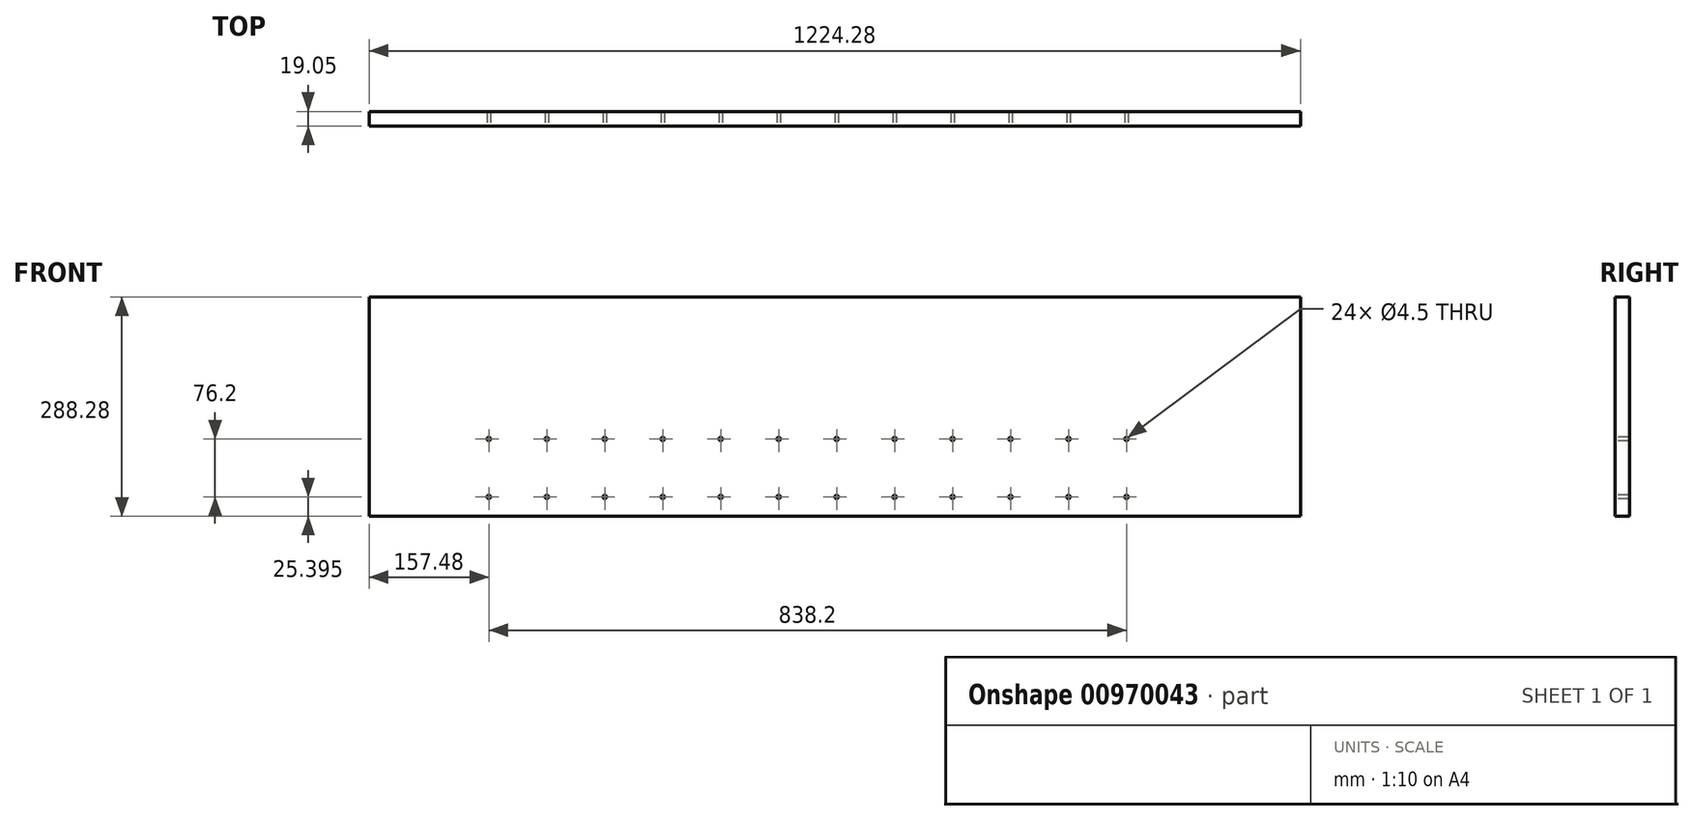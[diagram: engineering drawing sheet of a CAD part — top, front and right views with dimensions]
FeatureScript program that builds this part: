
annotation { "Feature Type Name" : "Feature", "Feature Type Description" : "" }
export const myFeature = defineFeature(function(context is Context, id is Id, definition is map)
    precondition{}
    {
        {
            var Q0;
            Q0=qCreatedBy(makeId("Front.planeOp"),FACE);
            var sketch = newSketch(context, id + "F0", { "sketchPlane" : qUnion([Q0])});
            skLineSegment(sketch, "E0.bottom", {"start": v(612.14, -144.14) * mm, "end": v(-612.14, -144.15) * mm});
            skLineSegment(sketch, "E0.top", {"start": v(612.14, 144.15) * mm, "end": v(-612.14, 144.15) * mm});
            skLineSegment(sketch, "E0.left", {"start": v(612.14, -144.14) * mm, "end": v(612.14, 144.15) * mm});
            skLineSegment(sketch, "E0.right", {"start": v(-612.14, -144.15) * mm, "end": v(-612.14, 144.14) * mm});
            skPoint(sketch, "E0.middle", {"position": v(0, 0) * mm});
            skSolve(sketch);
        }
        {
            var Q0;
            Q0=makeQuery(id+"F0.imprint","IMPRINT",FACE,{"disambiguationData":[TD([[makeQuery(id+"F0.imprint","IMPRINT",EDGE,{"derivedFrom":sQuery(id+"F0.wireOp",EDGE,"E0.bottom")}),-1.0]])]});
            extrude(context, id + "F1", {"entities" : qUnion([Q0]), "depth" : 19.05 * mm, "offsetDistance" : 25.4 * mm});
        }
        {
            var Q0;
            Q0=makeQuery(id+"F1.opExtrude","CAP_FACE",FACE,{"disambiguationData":[OSD([sQuery(id+"F0.wireOp",EDGE,"E0.bottom"),sQuery(id+"F0.wireOp",EDGE,"E0.top"),sQuery(id+"F0.wireOp",EDGE,"E0.left"),sQuery(id+"F0.wireOp",EDGE,"E0.right")])],"isStart":false});
            var sketch = newSketch(context, id + "F2", { "sketchPlane" : qUnion([Q0])});
            skLineSegment(sketch, "E1", {"start": v(-496.57, 144.15) * mm, "end": v(-496.57, -144.15) * mm, "construction": true});
            skLineSegment(sketch, "E2", {"start": v(425.45, 144.15) * mm, "end": v(425.45, -144.14) * mm, "construction": true});
            skLineSegment(sketch, "E3", {"start": v(-496.57, -42.55) * mm, "end": v(425.45, -42.55) * mm, "construction": true});
            skLineSegment(sketch, "E4", {"start": v(-35.56, -42.55) * mm, "end": v(-35.56, 387.93) * mm, "construction": true});
            skLineSegment(sketch, "E5", {"start": v(-35.56, -42.55) * mm, "end": v(-35.56, -118.75) * mm, "construction": true});
            skLineSegment(sketch, "E6", {"start": v(-496.57, -118.75) * mm, "end": v(425.45, -118.75) * mm, "construction": true});
            skLineSegment(sketch, "E7", {"start": v(-35.56, -80.65) * mm, "end": v(425.45, -80.65) * mm, "construction": true});
            skPoint(sketch, "E8", {"position": v(2.54, -42.55) * mm});
            skPoint(sketch, "E9", {"position": v(78.74, -42.55) * mm});
            skPoint(sketch, "E10", {"position": v(231.14, -42.55) * mm});
            skPoint(sketch, "E11", {"position": v(154.94, -42.55) * mm});
            skPoint(sketch, "E12", {"position": v(307.34, -42.55) * mm});
            skPoint(sketch, "E13", {"position": v(383.54, -42.55) * mm});
            skPoint(sketch, "E14.MirrorP", {"position": v(2.54, -118.75) * mm});
            skPoint(sketch, "E15.MirrorP", {"position": v(78.74, -118.75) * mm});
            skPoint(sketch, "E16.MirrorP", {"position": v(154.94, -118.75) * mm});
            skPoint(sketch, "E17.MirrorP", {"position": v(231.14, -118.75) * mm});
            skPoint(sketch, "E18.MirrorP", {"position": v(307.34, -118.75) * mm});
            skPoint(sketch, "E19.MirrorP", {"position": v(383.54, -118.75) * mm});
            skPoint(sketch, "E20.MirrorP", {"position": v(-73.66, -42.55) * mm});
            skPoint(sketch, "E21.MirrorP", {"position": v(-73.66, -118.75) * mm});
            skPoint(sketch, "E22.MirrorP", {"position": v(-149.86, -118.75) * mm});
            skPoint(sketch, "E23.MirrorP", {"position": v(-149.86, -42.55) * mm});
            skPoint(sketch, "E24.MirrorP", {"position": v(-226.06, -42.55) * mm});
            skPoint(sketch, "E25.MirrorP", {"position": v(-226.06, -118.75) * mm});
            skPoint(sketch, "E26.MirrorP", {"position": v(-302.26, -118.75) * mm});
            skPoint(sketch, "E27.MirrorP", {"position": v(-302.26, -42.55) * mm});
            skPoint(sketch, "E28.MirrorP", {"position": v(-378.46, -42.55) * mm});
            skPoint(sketch, "E29.MirrorP", {"position": v(-378.46, -118.75) * mm});
            skPoint(sketch, "E30.MirrorP", {"position": v(-454.66, -118.75) * mm});
            skPoint(sketch, "E31.MirrorP", {"position": v(-454.66, -42.55) * mm});
            skSolve(sketch);
        }
        {
            var Q0;
            Q0=sQuery(id+"F2.wireOp",VERTEX,"E13");
            var Q1;
            Q1=sQuery(id+"F2.wireOp",VERTEX,"E12");
            var Q2;
            Q2=sQuery(id+"F2.wireOp",VERTEX,"E10");
            var Q3;
            Q3=sQuery(id+"F2.wireOp",VERTEX,"E11");
            var Q4;
            Q4=sQuery(id+"F2.wireOp",VERTEX,"E9");
            var Q5;
            Q5=sQuery(id+"F2.wireOp",VERTEX,"E8");
            var Q6;
            Q6=sQuery(id+"F2.wireOp",VERTEX,"E20.MirrorP");
            var Q7;
            Q7=sQuery(id+"F2.wireOp",VERTEX,"E23.MirrorP");
            var Q8;
            Q8=sQuery(id+"F2.wireOp",VERTEX,"E24.MirrorP");
            var Q9;
            Q9=sQuery(id+"F2.wireOp",VERTEX,"E27.MirrorP");
            var Q10;
            Q10=sQuery(id+"F2.wireOp",VERTEX,"E28.MirrorP");
            var Q11;
            Q11=sQuery(id+"F2.wireOp",VERTEX,"E31.MirrorP");
            var Q12;
            Q12=sQuery(id+"F2.wireOp",VERTEX,"E30.MirrorP");
            var Q13;
            Q13=sQuery(id+"F2.wireOp",VERTEX,"E29.MirrorP");
            var Q14;
            Q14=sQuery(id+"F2.wireOp",VERTEX,"E26.MirrorP");
            var Q15;
            Q15=sQuery(id+"F2.wireOp",VERTEX,"E25.MirrorP");
            var Q16;
            Q16=sQuery(id+"F2.wireOp",VERTEX,"E22.MirrorP");
            var Q17;
            Q17=sQuery(id+"F2.wireOp",VERTEX,"E21.MirrorP");
            var Q18;
            Q18=sQuery(id+"F2.wireOp",VERTEX,"E14.MirrorP");
            var Q19;
            Q19=sQuery(id+"F2.wireOp",VERTEX,"E15.MirrorP");
            var Q20;
            Q20=sQuery(id+"F2.wireOp",VERTEX,"E16.MirrorP");
            var Q21;
            Q21=sQuery(id+"F2.wireOp",VERTEX,"E17.MirrorP");
            var Q22;
            Q22=sQuery(id+"F2.wireOp",VERTEX,"E18.MirrorP");
            var Q23;
            Q23=sQuery(id+"F2.wireOp",VERTEX,"E19.MirrorP");
            var Q24;
            Q24=makeQuery(id+"F1.opExtrude","SWEPT_BODY",BODY,{"disambiguationData":[OSD([sQuery(id+"F0.wireOp",EDGE,"E0.bottom"),sQuery(id+"F0.wireOp",EDGE,"E0.top"),sQuery(id+"F0.wireOp",EDGE,"E0.left"),sQuery(id+"F0.wireOp",EDGE,"E0.right")])]});
            hole(context, id + "F3", {"style" : HoleStyle.SIMPLE, "endStyle" : HoleEndStyle.THROUGH, "standardTappedOrClearance" : lookupTablePath({ "standard" : "ANSI", "fit" : "Normal (ASME)", "size" : "#8", "type" : "Clearance" }), "standardBlindInLast" : lookupTablePath({ "fit" : "Free", "standard" : "ANSI", "size" : "#8", "type" : "Clearance" }), "holeDiameter" : 4.5 * mm, "majorDiameter" : 4.17 * mm, "isTappedThrough" : true, "tappedDepth" : 12.7 * mm, "tapClearance" : 3, "locations" : qUnion([Q0, Q1, Q2, Q3, Q4, Q5, Q6, Q7, Q8, Q9, Q10, Q11, Q12, Q13, Q14, Q15, Q16, Q17, Q18, Q19, Q20, Q21, Q22, Q23]), "scope" : qUnion([Q24])});
        }
    });
